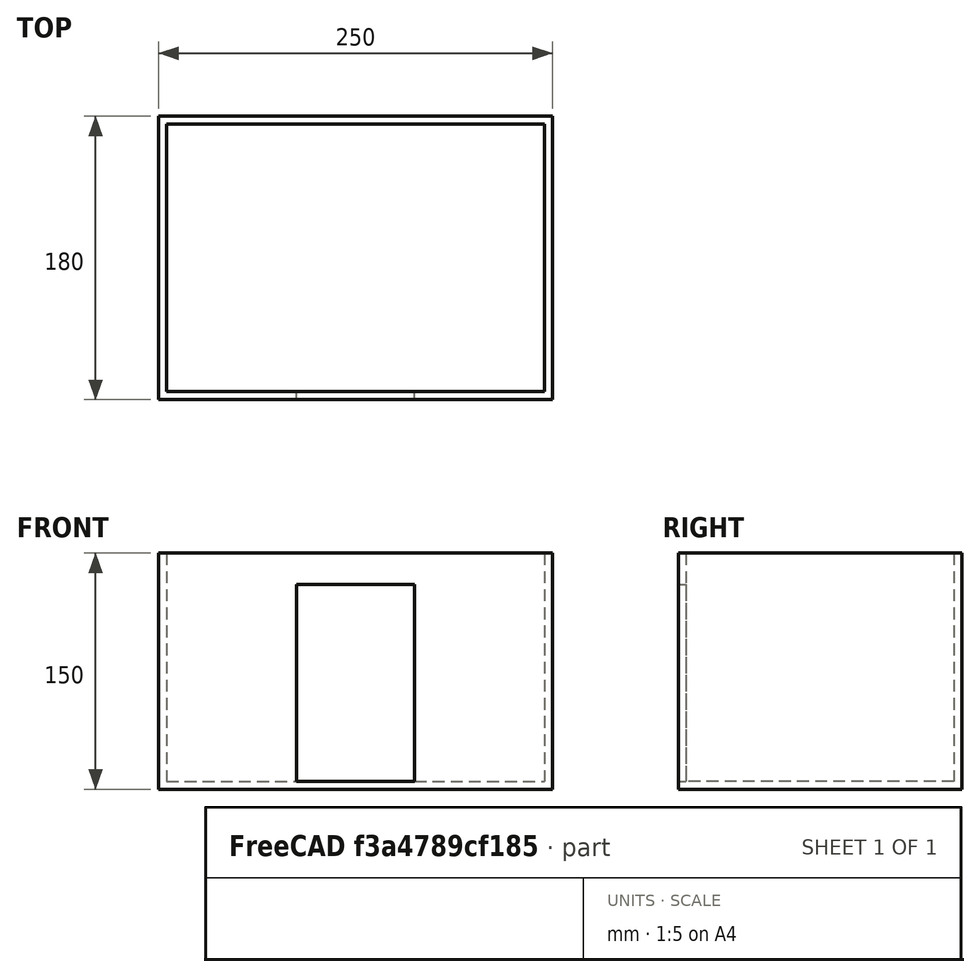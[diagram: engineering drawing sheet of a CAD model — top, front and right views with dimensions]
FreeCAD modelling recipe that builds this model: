
FCSTD DOCUMENT  (FreeCAD 0.19R24267 +148 (Git))
Label: Kasten
License: All rights reserved
LicenseURL: http://en.wikipedia.org/wiki/All_rights_reserved
objects: TechDraw::DrawViewDimension×16, TechDraw::DrawProjGroupItem×5, Sketcher::SketchObject×3, PartDesign::Pocket×2, PartDesign::Pad×1, PartDesign::Body×1, TechDraw::DrawSVGTemplate×1, TechDraw::DrawProjGroup×1, TechDraw::DrawViewPart×1, TechDraw::DrawPage×1
note: 10 computed .brp shape members not serialized (recipe doc carries the construction recipe); baked Part::Feature solids carry a one-line shape summary decoded from their .brp

FEATURE [Sketcher::SketchObject] Sketch
  FullyConstrained = true
  MapMode = 5
  Support = -> [XY_Plane]
  sketch-geometry (4):
    g0: LineSegment StartX=0 StartY=180 StartZ=0 EndX=250 EndY=180 EndZ=0
    g1: LineSegment StartX=250 StartY=180 StartZ=0 EndX=250 EndY=0 EndZ=0
    g2: LineSegment StartX=250 StartY=0 StartZ=0 EndX=0 EndY=0 EndZ=0
    g3: LineSegment StartX=0 StartY=0 StartZ=0 EndX=0 EndY=180 EndZ=0
  constraints (11):
    c: Coincident(g0,g1)
    c: Coincident(g1,g2)
    c: Coincident(g2,g3)
    c: Coincident(g3,g0)
    c: Horizontal(g0)
    c: Horizontal(g2)
    c: Vertical(g1)
    c: Vertical(g3)
    c: DistanceY(g2,g0) = 180
    c: DistanceX(g0,g0) = 250
    c: Coincident(g2,g-1)
FEATURE [PartDesign::Pad] Pad
  Direction = (1,1,1)
  Length = 150
  Length2 = 100
  Profile = -> Sketch
  Type = 0
FEATURE [Sketcher::SketchObject] Sketch001
  ExternalGeometry = -> [Pad]
  FullyConstrained = true
  MapMode = 5
  Placement = pos=(0,0,150) rot=(0,0,1;0rad)
  Support = -> [Pad]
  sketch-geometry (6):
    g0: LineSegment StartX=5 StartY=175 StartZ=0 EndX=245 EndY=175 EndZ=0
    g1: LineSegment StartX=245 StartY=175 StartZ=0 EndX=245 EndY=5 EndZ=0
    g2: LineSegment StartX=245 StartY=5 StartZ=0 EndX=5 EndY=5 EndZ=0
    g3: LineSegment StartX=5 StartY=5 StartZ=0 EndX=5 EndY=175 EndZ=0
    g4: LineSegment StartX=125 StartY=180 StartZ=0 EndX=125 EndY=0 EndZ=0
    g5: LineSegment StartX=0 StartY=90 StartZ=0 EndX=250 EndY=90 EndZ=0
  constraints (16):
    c: Coincident(g0,g1)
    c: Coincident(g1,g2)
    c: Coincident(g2,g3)
    c: Coincident(g3,g0)
    c: Horizontal(g2)
    c: Vertical(g1)
    c: PointOnObject(g4,g-3)
    c: Symmetric(g-6,g-1,g4)
    c: Vertical(g4)
    c: Symmetric(g0,g0,g4)
    c: PointOnObject(g5,g-4)
    c: Horizontal(g5)
    c: Symmetric(g-5,g-6,g5)
    c: Symmetric(g0,g2,g5)
    c: DistanceX(g-1,g2) = 5
    c: DistanceY(g2) = 5
FEATURE [PartDesign::Pocket] Pocket
  BaseFeature = -> Pad
  Length = 145
  Length2 = 100
  Profile = -> Sketch001
  Type = 0
FEATURE [Sketcher::SketchObject] Sketch002
  ExternalGeometry = -> [Pocket]
  FullyConstrained = true
  MapMode = 5
  Placement = pos=(0,0,0) rot=(1,0,0;1.5708rad)
  Support = -> [Pocket]
  sketch-geometry (5):
    g0: LineSegment StartX=87.5 StartY=130 StartZ=0 EndX=162.5 EndY=130 EndZ=0
    g1: LineSegment StartX=162.5 StartY=130 StartZ=0 EndX=162.5 EndY=5 EndZ=0
    g2: LineSegment StartX=162.5 StartY=5 StartZ=0 EndX=87.5 EndY=5 EndZ=0
    g3: LineSegment StartX=87.5 StartY=5 StartZ=0 EndX=87.5 EndY=130 EndZ=0
    g4: LineSegment StartX=125 StartY=150 StartZ=0 EndX=125 EndY=0 EndZ=0
  constraints (14):
    c: Coincident(g0,g1)
    c: Coincident(g1,g2)
    c: Coincident(g2,g3)
    c: Coincident(g3,g0)
    c: Horizontal(g2)
    c: Vertical(g1)
    c: Vertical(g3)
    c: PointOnObject(g4,g-4)
    c: Symmetric(g-1,g-5,g4)
    c: Vertical(g4)
    c: Symmetric(g0,g0,g4)
    c: DistanceY(g0,g4) = 20
    c: DistanceY(g4,g2) = 5
    c: DistanceX(g0,g0) = 75
FEATURE [PartDesign::Pocket] Pocket001
  BaseFeature = -> Pocket
  Length = 5
  Length2 = 100
  Profile = -> Sketch002
  Type = 0
FEATURE [PartDesign::Body] Body
  Group = -> [Sketch,Pad,Sketch001,Pocket,Sketch002,Pocket001]
  Origin = -> Origin
  Tip = -> Pocket001
FEATURE [TechDraw::DrawSVGTemplate] Template
  EditableTexts = Designed_by_Name=Designed by Name; Drawing_number=Drawing number; FC-Date=Date; FC-SC=1:5; FC-SH=Sheet; FC-Title=Title; Subtitle=Subtitle; Weight=Weight
  Height = 210
  Orientation = 1
  Width = 297
FEATURE [TechDraw::DrawProjGroupItem] ProjItem  label="Front"
  CoarseView = false
  Direction = (0,-1,0)
  Focus = 100
  HardHidden = false
  IsoCount = 0
  IsoHidden = false
  IsoVisible = false
  LockPosition = true
  Perspective = false
  Rotation = 0
  RotationVector = (1,0,0)
  Scale = 0.2
  ScaleType = 2
  SeamHidden = false
  SeamVisible = true
  SmoothHidden = false
  SmoothVisible = true
  Source = -> [Body]
  Type = 0
  X = 0
  XDirection = (1,0,0)
  Y = 0
FEATURE [TechDraw::DrawProjGroupItem] ProjItem001  label="Left"
  CoarseView = false
  Direction = (-1,-1e-16,0)
  Focus = 100
  HardHidden = false
  IsoCount = 0
  IsoHidden = false
  IsoVisible = false
  LockPosition = false
  Perspective = false
  Rotation = 0
  RotationVector = (1,0,0)
  Scale = 0.2
  ScaleType = 2
  SeamHidden = false
  SeamVisible = true
  SmoothHidden = false
  SmoothVisible = true
  Source = -> [Body]
  Type = 1
  X = 58
  XDirection = (1e-16,-1,0)
  Y = 0
FEATURE [TechDraw::DrawProjGroupItem] ProjItem002  label="Bottom"
  CoarseView = false
  Direction = (0,0,-1)
  Focus = 100
  HardHidden = false
  IsoCount = 0
  IsoHidden = false
  IsoVisible = false
  LockPosition = false
  Perspective = false
  Rotation = 0
  RotationVector = (1,0,0)
  Scale = 0.2
  ScaleType = 2
  SeamHidden = false
  SeamVisible = true
  SmoothHidden = false
  SmoothVisible = true
  Source = -> [Body]
  Type = 5
  X = 0
  XDirection = (1,0,0)
  Y = 51
FEATURE [TechDraw::DrawProjGroupItem] ProjItem003  label="Top"
  CoarseView = false
  Direction = (0,0,1)
  Focus = 100
  HardHidden = false
  IsoCount = 0
  IsoHidden = false
  IsoVisible = false
  LockPosition = false
  Perspective = false
  Rotation = 0
  RotationVector = (1,0,0)
  Scale = 0.2
  ScaleType = 2
  SeamHidden = false
  SeamVisible = true
  SmoothHidden = false
  SmoothVisible = true
  Source = -> [Body]
  Type = 4
  X = 0
  XDirection = (1,0,0)
  Y = -51
FEATURE [TechDraw::DrawProjGroupItem] ProjItem004  label="Rear"
  CoarseView = false
  Direction = (0,1,0)
  Focus = 100
  HardHidden = false
  IsoCount = 0
  IsoHidden = false
  IsoVisible = false
  LockPosition = false
  Perspective = false
  Rotation = 0
  RotationVector = (1,0,0)
  Scale = 0.2
  ScaleType = 2
  SeamHidden = false
  SeamVisible = true
  SmoothHidden = false
  SmoothVisible = true
  Source = -> [Body]
  Type = 3
  X = 123
  XDirection = (-1,0,0)
  Y = 0
FEATURE [TechDraw::DrawProjGroup] ProjGroup
  Anchor = -> ProjItem
  AutoDistribute = true
  LockPosition = false
  ProjectionType = 0
  Rotation = 0
  Scale = 0.2
  ScaleType = 2
  Source = -> [Body]
  Views = -> [ProjItem,ProjItem001,ProjItem002,ProjItem003,ProjItem004]
  X = 87.265
  Y = 110.403
  spacingX = 15
  spacingY = 15
FEATURE [TechDraw::DrawViewPart] View
  CoarseView = false
  Direction = (0.577,-0.577,0.577)
  Focus = 100
  HardHidden = false
  IsoCount = 0
  IsoHidden = false
  IsoVisible = false
  LockPosition = false
  Perspective = false
  Rotation = 0
  Scale = 0.2
  ScaleType = 0
  SeamHidden = false
  SeamVisible = true
  SmoothHidden = false
  SmoothVisible = true
  Source = -> [Body]
  X = 252.239
  XDirection = (0.707,0.707,0)
  Y = 174.52
FEATURE [TechDraw::DrawViewDimension] Dimension
  Arbitrary = false
  ArbitraryTolerances = false
  EqualTolerance = true
  FormatSpec = %.2f
  FormatSpecOverTolerance = %+.2f
  FormatSpecUnderTolerance = %+.2f
  Inverted = false
  LockPosition = false
  MeasureType = 1
  OverTolerance = 0
  References2D = -> [ProjItem004]
  Rotation = 0
  ScaleType = 0
  TheoreticalExact = false
  Type = 1
  UnderTolerance = 0
  X = 1.80103
  Y = -24.0051
FEATURE [TechDraw::DrawViewDimension] Dimension001
  Arbitrary = false
  ArbitraryTolerances = false
  EqualTolerance = true
  FormatSpec = %.2f
  FormatSpecOverTolerance = %+.2f
  FormatSpecUnderTolerance = %+.2f
  Inverted = false
  LockPosition = false
  MeasureType = 1
  OverTolerance = 0
  References2D = -> [ProjItem004]
  Rotation = 0
  ScaleType = 0
  TheoreticalExact = false
  Type = 2
  UnderTolerance = 0
  X = 39.4082
  Y = -1.44082
FEATURE [TechDraw::DrawViewDimension] Dimension002
  Arbitrary = false
  ArbitraryTolerances = false
  EqualTolerance = true
  FormatSpec = %.2f
  FormatSpecOverTolerance = %+.2f
  FormatSpecUnderTolerance = %+.2f
  Inverted = false
  LockPosition = false
  MeasureType = 1
  OverTolerance = 0
  References2D = -> [ProjItem001]
  Rotation = 0
  ScaleType = 0
  TheoreticalExact = false
  Type = 1
  UnderTolerance = 0
  X = 3.96226
  Y = -25.446
FEATURE [TechDraw::DrawViewDimension] Dimension003
  Arbitrary = false
  ArbitraryTolerances = false
  EqualTolerance = true
  FormatSpec = %.2f
  FormatSpecOverTolerance = %+.2f
  FormatSpecUnderTolerance = %+.2f
  Inverted = false
  LockPosition = false
  MeasureType = 1
  OverTolerance = 0
  References2D = -> [ProjItem001]
  Rotation = 0
  ScaleType = 0
  TheoreticalExact = false
  Type = 2
  UnderTolerance = 0
  X = 30.247
  Y = -2.16124
FEATURE [TechDraw::DrawViewDimension] Dimension004
  Arbitrary = false
  ArbitraryTolerances = false
  EqualTolerance = true
  FormatSpec = %.2f
  FormatSpecOverTolerance = %+.2f
  FormatSpecUnderTolerance = %+.2f
  Inverted = false
  LockPosition = false
  MeasureType = 1
  OverTolerance = 0
  References2D = -> [ProjItem003]
  Rotation = 0
  ScaleType = 0
  TheoreticalExact = false
  Type = 2
  UnderTolerance = 0
  X = 28.4373
  Y = -9.20654
FEATURE [TechDraw::DrawViewDimension] Dimension005
  Arbitrary = false
  ArbitraryTolerances = false
  EqualTolerance = true
  FormatSpec = %.2f
  FormatSpecOverTolerance = %+.2f
  FormatSpecUnderTolerance = %+.2f
  Inverted = false
  LockPosition = false
  MeasureType = 1
  OverTolerance = 0
  References2D = -> [ProjItem003]
  Rotation = 0
  ScaleType = 0
  TheoreticalExact = false
  Type = 2
  UnderTolerance = 0
  X = 36.4794
  Y = -6.53161
FEATURE [TechDraw::DrawViewDimension] Dimension006
  Arbitrary = false
  ArbitraryTolerances = false
  EqualTolerance = true
  FormatSpec = %.2f
  FormatSpecOverTolerance = %+.2f
  FormatSpecUnderTolerance = %+.2f
  Inverted = false
  LockPosition = false
  MeasureType = 1
  OverTolerance = 0
  References2D = -> [ProjItem003]
  Rotation = 0
  ScaleType = 0
  TheoreticalExact = false
  Type = 2
  UnderTolerance = 0
  X = 46.2782
  Y = -0.418862
FEATURE [TechDraw::DrawViewDimension] Dimension007
  Arbitrary = false
  ArbitraryTolerances = false
  EqualTolerance = true
  FormatSpec = %.2f
  FormatSpecOverTolerance = %+.2f
  FormatSpecUnderTolerance = %+.2f
  Inverted = false
  LockPosition = false
  MeasureType = 1
  OverTolerance = 0
  References2D = -> [ProjItem003]
  Rotation = 0
  ScaleType = 0
  TheoreticalExact = false
  Type = 1
  UnderTolerance = 0
  X = 16.7795
  Y = -19.4301
FEATURE [TechDraw::DrawViewDimension] Dimension008
  Arbitrary = false
  ArbitraryTolerances = false
  EqualTolerance = true
  FormatSpec = %.2f
  FormatSpecOverTolerance = %+.2f
  FormatSpecUnderTolerance = %+.2f
  Inverted = false
  LockPosition = false
  MeasureType = 1
  OverTolerance = 0
  References2D = -> [ProjItem003]
  Rotation = 0
  ScaleType = 0
  TheoreticalExact = false
  Type = 1
  UnderTolerance = 0
  X = 2.06822
  Y = -26.9093
FEATURE [TechDraw::DrawViewDimension] Dimension009
  Arbitrary = false
  ArbitraryTolerances = false
  EqualTolerance = true
  FormatSpec = %.2f
  FormatSpecOverTolerance = %+.2f
  FormatSpecUnderTolerance = %+.2f
  Inverted = false
  LockPosition = false
  MeasureType = 1
  OverTolerance = 0
  References2D = -> [ProjItem003]
  Rotation = 0
  ScaleType = 0
  TheoreticalExact = false
  Type = 1
  UnderTolerance = 0
  X = 2.19214
  Y = -35.5371
FEATURE [TechDraw::DrawViewDimension] Dimension010
  Arbitrary = false
  ArbitraryTolerances = false
  EqualTolerance = true
  FormatSpec = %.2f
  FormatSpecOverTolerance = %+.2f
  FormatSpecUnderTolerance = %+.2f
  Inverted = false
  LockPosition = false
  MeasureType = 1
  OverTolerance = 0
  References2D = -> [ProjItem]
  Rotation = 0
  ScaleType = 0
  TheoreticalExact = false
  Type = 1
  UnderTolerance = 0
  X = -14.6059
  Y = -16.4181
FEATURE [TechDraw::DrawViewDimension] Dimension011
  Arbitrary = false
  ArbitraryTolerances = false
  EqualTolerance = true
  FormatSpec = %.2f
  FormatSpecOverTolerance = %+.2f
  FormatSpecUnderTolerance = %+.2f
  Inverted = false
  LockPosition = false
  MeasureType = 1
  OverTolerance = 0
  References2D = -> [ProjItem]
  Rotation = 0
  ScaleType = 0
  TheoreticalExact = false
  Type = 1
  UnderTolerance = 0
  X = 0.29259
  Y = -21.3504
FEATURE [TechDraw::DrawViewDimension] Dimension012
  Arbitrary = false
  ArbitraryTolerances = false
  EqualTolerance = true
  FormatSpec = %.2f
  FormatSpecOverTolerance = %+.2f
  FormatSpecUnderTolerance = %+.2f
  Inverted = false
  LockPosition = false
  MeasureType = 1
  OverTolerance = 0
  References2D = -> [ProjItem]
  Rotation = 0
  ScaleType = 0
  TheoreticalExact = false
  Type = 0
  UnderTolerance = 0
  X = -1.64411
  Y = -28.7009
FEATURE [TechDraw::DrawViewDimension] Dimension013
  Arbitrary = false
  ArbitraryTolerances = false
  EqualTolerance = true
  FormatSpec = %.2f
  FormatSpecOverTolerance = %+.2f
  FormatSpecUnderTolerance = %+.2f
  Inverted = false
  LockPosition = false
  MeasureType = 1
  OverTolerance = 0
  References2D = -> [ProjItem]
  Rotation = 0
  ScaleType = 0
  TheoreticalExact = false
  Type = 2
  UnderTolerance = 0
  X = -31.869
  Y = -6.27946
FEATURE [TechDraw::DrawViewDimension] Dimension014
  Arbitrary = false
  ArbitraryTolerances = false
  EqualTolerance = true
  FormatSpec = %.2f
  FormatSpecOverTolerance = %+.2f
  FormatSpecUnderTolerance = %+.2f
  Inverted = false
  LockPosition = false
  MeasureType = 1
  OverTolerance = 0
  References2D = -> [ProjItem]
  Rotation = 0
  ScaleType = 0
  TheoreticalExact = false
  Type = 2
  UnderTolerance = 0
  X = -40.3636
  Y = -1.17795
FEATURE [TechDraw::DrawViewDimension] Dimension015
  Arbitrary = false
  ArbitraryTolerances = false
  EqualTolerance = true
  FormatSpec = %.2f
  FormatSpecOverTolerance = %+.2f
  FormatSpecUnderTolerance = %+.2f
  Inverted = false
  LockPosition = false
  MeasureType = 1
  OverTolerance = 0
  References2D = -> [ProjItem]
  Rotation = 0
  ScaleType = 0
  TheoreticalExact = false
  Type = 2
  UnderTolerance = 0
  X = -50.2096
  Y = 3.28821
FEATURE [TechDraw::DrawPage] Page
  KeepUpdated = true
  NextBalloonIndex = 1
  ProjectionType = 0
  Template = -> Template
  Views = -> [ProjGroup,View,Dimension,Dimension001,Dimension002,Dimension003,Dimension004,Dimension005,Dimension006,Dimension007,Dimension008,Dimension009,Dimension010,Dimension011,Dimension012,Dimension013,Dimension014,Dimension015]
